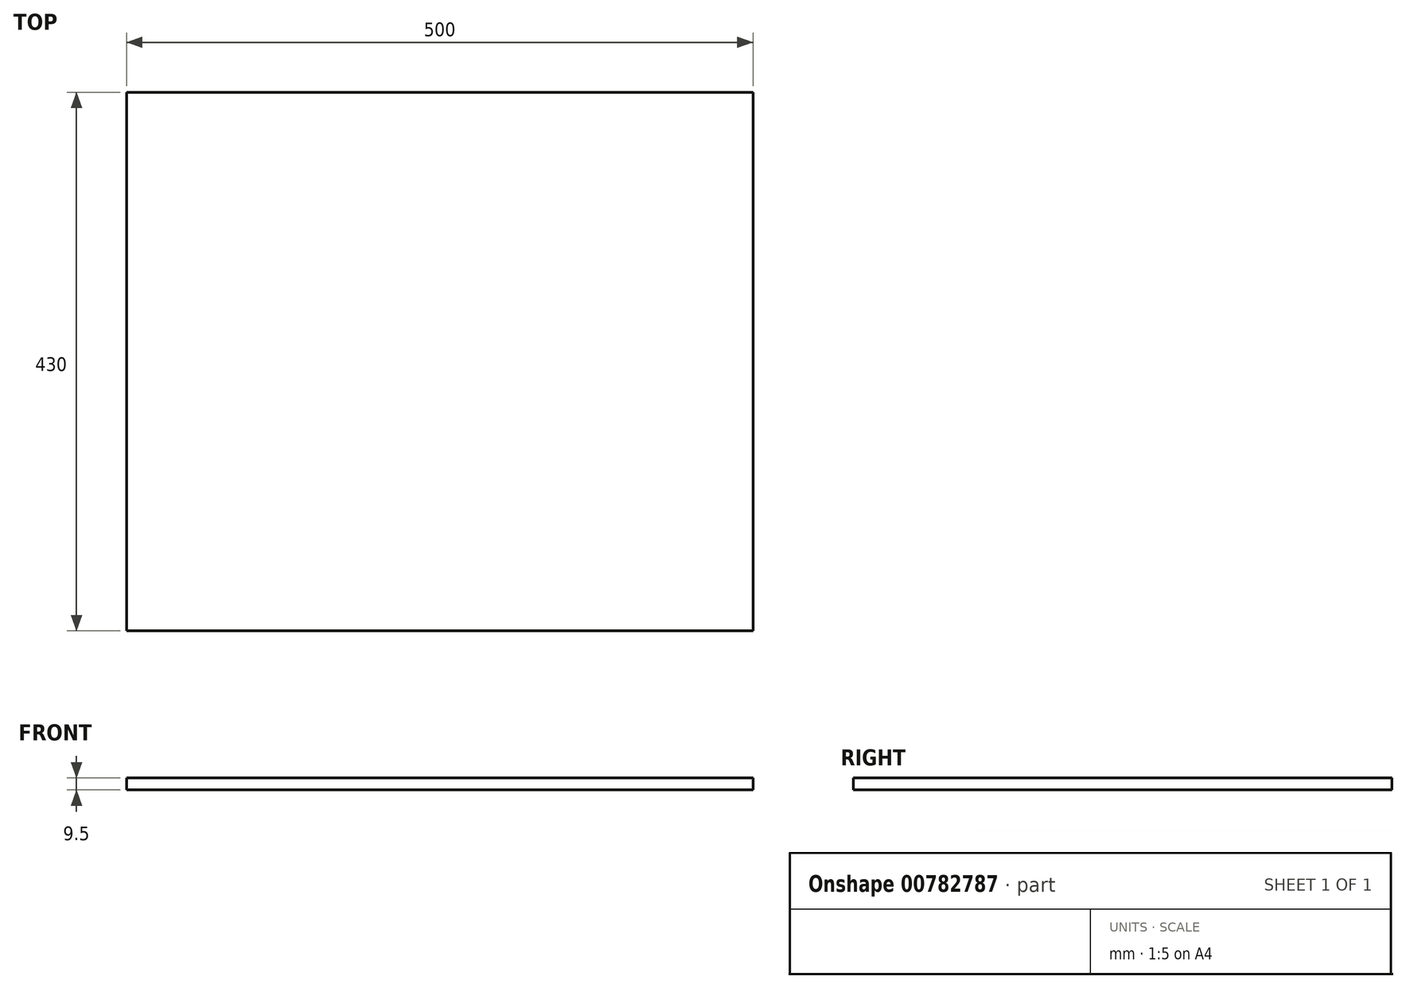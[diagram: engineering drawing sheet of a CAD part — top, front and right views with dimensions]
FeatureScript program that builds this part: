
annotation { "Feature Type Name" : "Feature", "Feature Type Description" : "" }
export const myFeature = defineFeature(function(context is Context, id is Id, definition is map)
    precondition{}
    {
        {
            var Q0;
            Q0=qCreatedBy(makeId("Top.planeOp"),FACE);
            var sketch = newSketch(context, id + "F0", { "sketchPlane" : qUnion([Q0])});
            skLineSegment(sketch, "E0.bottom", {"start": v(-35.8, -23.78) * mm, "end": v(464.2, -23.78) * mm});
            skLineSegment(sketch, "E0.top", {"start": v(-35.8, 406.22) * mm, "end": v(464.2, 406.22) * mm});
            skLineSegment(sketch, "E0.left", {"start": v(-35.8, -23.78) * mm, "end": v(-35.8, 406.22) * mm});
            skLineSegment(sketch, "E0.right", {"start": v(464.2, -23.78) * mm, "end": v(464.2, 406.22) * mm});
            skSolve(sketch);
        }
        {
            var Q0;
            Q0=makeQuery(id+"F0.imprint","IMPRINT",FACE,{"disambiguationData":[TD([[makeQuery(id+"F0.imprint","IMPRINT",EDGE,{"derivedFrom":sQuery(id+"F0.wireOp",EDGE,"E0.bottom")}),1.0]])]});
            extrude(context, id + "F1", {"entities" : qUnion([Q0]), "depth" : 9.5 * mm, "offsetDistance" : 25 * mm});
        }
    });
